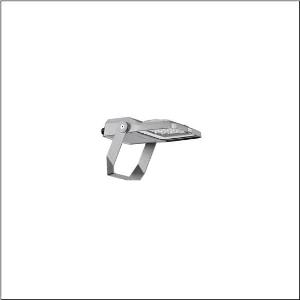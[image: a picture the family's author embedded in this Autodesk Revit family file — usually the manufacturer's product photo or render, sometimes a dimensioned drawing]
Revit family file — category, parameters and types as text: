
# Revit family: floodlight_fl_21_iq_micro___rs12_5xa7762a1b1a_c11c
name_source: partatom
category: Lighting Fixtures
units: mm (PartAtom-declared; Revit-internal decimal feet)

## family parameters
Cut with Voids When Loaded = No
Host = Face
Light Source = No
Part Type = Normal
Room Calculation Point = No
Round Connector Dimension = Use Diameter
Shared = No

## types (1)
- --- (1 x LED, 2560 lm, 23.1 W, 2200K)
    Apparent Load = 23 VA
    CIE Flux Codes = 79 92 99 100 100
    Color Rendering = 70
    Color Temperature = 2200K
    Default Elevation = 1800 mm
    Description = Floodlight FL 21 iQ micro, floodlight, primary light control with lens, of PMMA, primary optical cover: protective disc, of toughened safety glass, transparent, light distribution: RS12, light emission: direct distribution, installation type: surface-mounted, LED, High Power LED, rated luminous flux: 2.560lm, luminous efficacy: 111lm/W, light colour: 722, colour temperature: 2200K, control: Auto-Match, Temp-Guard, Night-Set, Smart-Wire, Desk-Remote (wireless, voltage-free reading and setting of iQ features in the workshop via application-optimized NFC function/RFID function), optimised constant luminous flux control (CLO 2.0), Street-Remote, with terminal, 6-pole, mains connection: 220..240V, AC, 50/60Hz, start of lifetime: 23W, end of service life: 24W, reduction: 11W, luminaire housing, of diecast aluminium, powder-coated, Siteco® metallic grey (DB 702S), corrosivity category C5 mid according to DIN EN ISO 12944, sealing non-destructively replaceable, mounting bracket, of steel, galvanised, powder-coated, Siteco® metallic grey (DB 702S), protection rating (complete): IP66, insulation class (complete): insulation class II (safety insulation), certification: CE, ENEC, VDE, protection symbol: D, impact resistance: IK07, permissible operating ambient temperature: -40..+40°C, permissible operating ambient temperature for outdoor applications: -40..+50°C, standard: DIN EN 12944, LABS conformity tested according to VDMA 24364:2018-05, packaging unit: 1 piece

Light Distribution: RS12
    Height = 65 mm
    Lamp = 1 x LED
    Lamp Light Flux = 2560 lm
    Lamp Power = 23.1 W
    Lamp count = 1
    Length = 312 mm
    Luminous efficacy = 111 lm/W
    Manufacturer = Siteco
    ModVariant = No
    Model = 5XA7762A1B1A
    Number of Poles = 1
    OnlyDefault = Yes
    Power Factor = 1
    Product Name = Floodlight FL 21 iQ micro | RS12
    Product group = floodlight | pylon annexe
    ProductGroupID = 6200
    Protection Class = Protection class II
    Protection Degree = IP 66
    RLX_Detail_Level = 1
    RLX_Emergency_Light_Flux = 0 lm
    RLX_Emergency_Type = 0
    RLX_Emergency_Type_DB = No
    RlxData = <blob elided: 74989 chars, md5=92629da1>
    Socket = socket
    Standby Power = 0 W
    System Light Flux = 2560 lm
    System Power = 23 W
    Type Comments = factory setting: luminous flux: 100 % | dim-lin: 254 | 455 mA
    Type Image = l_1006880.jpg
    URL = http://relux.com
    VarID = @adj_114973
    Voltage = 0 V
    Weight = 0.00 kg
    Width = 230 mm

## geometry (parser evidence)
native form markers: Blend x4, Sweep x12
no freeform markers — native parametric forms only
